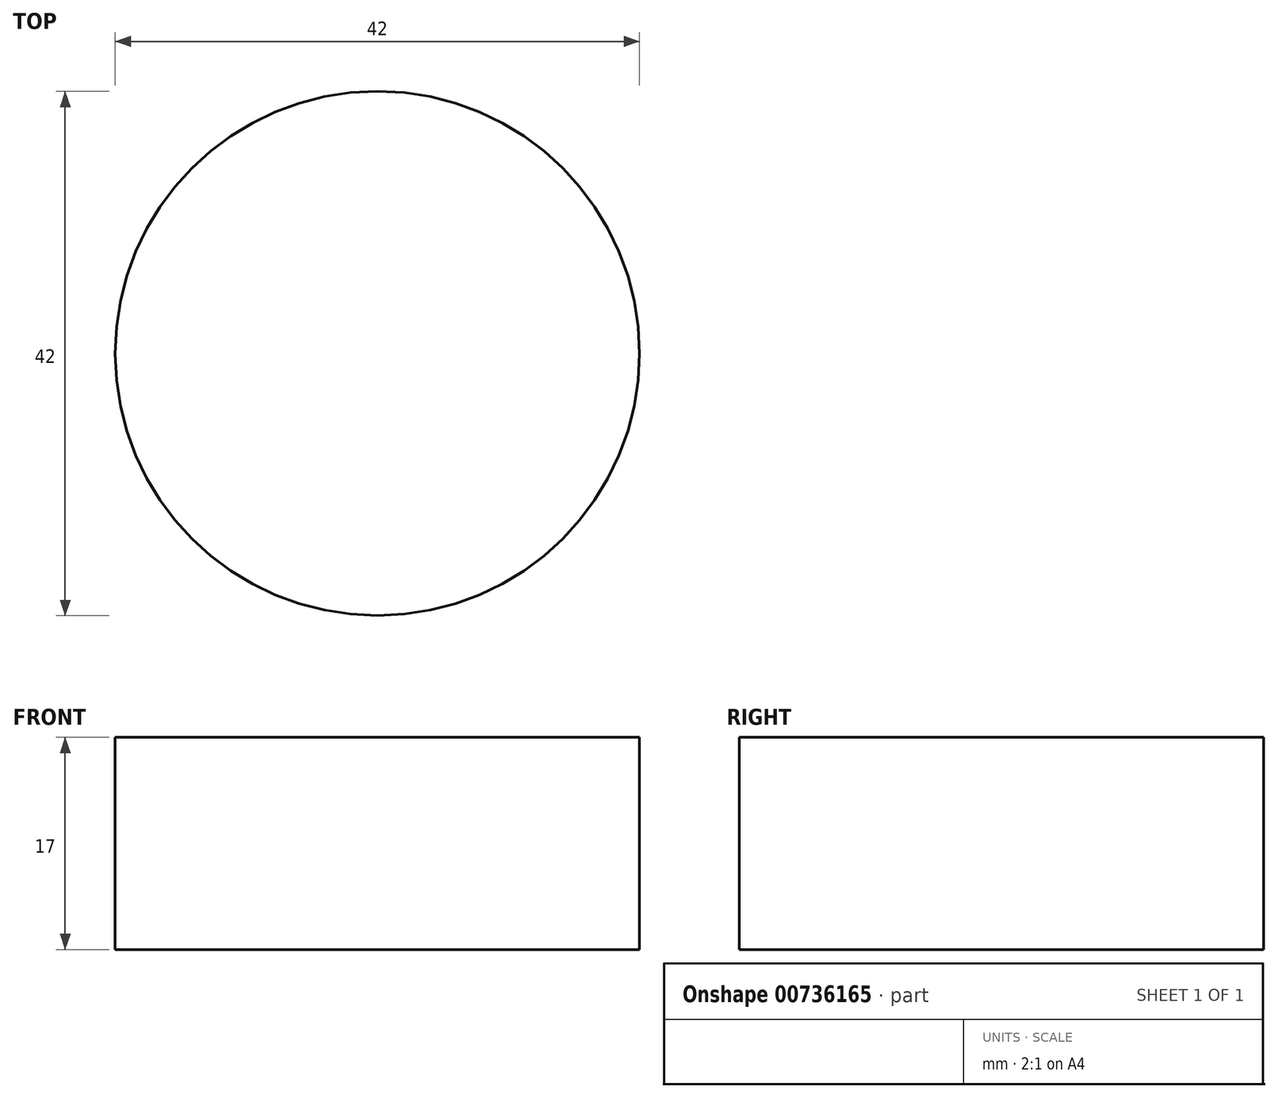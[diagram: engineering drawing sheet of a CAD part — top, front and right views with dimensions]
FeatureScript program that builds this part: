
annotation { "Feature Type Name" : "Feature", "Feature Type Description" : "" }
export const myFeature = defineFeature(function(context is Context, id is Id, definition is map)
    precondition{}
    {
        {
            var Q0;
            Q0=qCreatedBy(makeId("Top.planeOp"),FACE);
            var sketch = newSketch(context, id + "F0", { "sketchPlane" : qUnion([Q0])});
            skCircle(sketch, "E0", {"center": v(-21.14, -20.96) * mm, "radius": 21 * mm});
            skSolve(sketch);
        }
        {
            var Q0;
            Q0=makeQuery(id+"F0.imprint","IMPRINT",FACE,{"disambiguationData":[TD([[makeQuery(id+"F0.imprint","IMPRINT",EDGE,{"derivedFrom":sQuery(id+"F0.wireOp",EDGE,"E0")}),1.0]])]});
            extrude(context, id + "F1", {"entities" : qUnion([Q0]), "depth" : 17 * mm, "offsetDistance" : 25.4 * mm});
        }
    });
